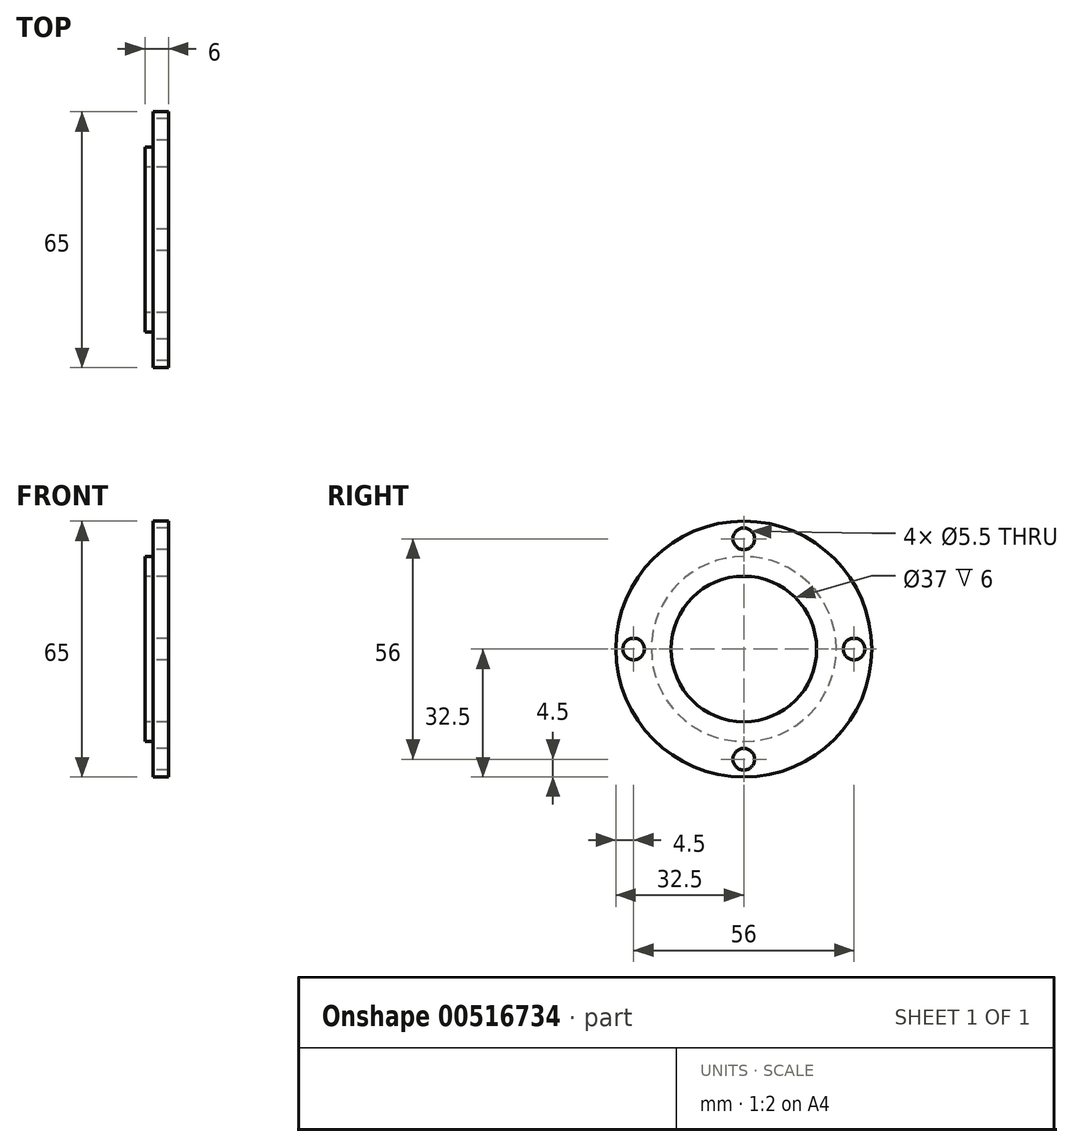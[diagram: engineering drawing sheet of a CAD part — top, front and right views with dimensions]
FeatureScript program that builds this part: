
annotation { "Feature Type Name" : "Feature", "Feature Type Description" : "" }
export const myFeature = defineFeature(function(context is Context, id is Id, definition is map)
    precondition{}
    {
        {
            var Q0;
            Q0=qCreatedBy(makeId("Front.planeOp"),FACE);
            var sketch = newSketch(context, id + "F0", { "sketchPlane" : qUnion([Q0])});
            skLineSegment(sketch, "E0", {"start": v(-34.12, 0) * mm, "end": v(37.4, 0) * mm, "construction": true});
            skLineSegment(sketch, "E1", {"start": v(0, 32.5) * mm, "end": v(0, 23.5) * mm});
            skLineSegment(sketch, "E2", {"start": v(4, 18.5) * mm, "end": v(4, 32.5) * mm});
            skLineSegment(sketch, "E3", {"start": v(4, 32.5) * mm, "end": v(0, 32.5) * mm});
            skLineSegment(sketch, "E4", {"start": v(4, 18.5) * mm, "end": v(-2, 18.5) * mm});
            skLineSegment(sketch, "E5", {"start": v(0, 23.5) * mm, "end": v(-2, 23.5) * mm});
            skLineSegment(sketch, "E6", {"start": v(-2, 23.5) * mm, "end": v(-2, 18.5) * mm});
            skSolve(sketch);
        }
        {
            var Q0;
            Q0=qSketchRegion(id+"F0",true);
            var Q1;
            Q1=sQuery(id+"F0.wireOp",EDGE,"E0");
            revolve(context, id + "F1", {"entities" : qUnion([Q0]), "axis" : qUnion([Q1]), "revolveType" : RevolveType.FULL});
        }
        {
            var Q0;
            Q0=makeQuery(id+"F1.opRevolve","SWEPT_FACE",FACE,{"disambiguationData":[OSD([sQuery(id+"F0.wireOp",EDGE,"E1")])]});
            var sketch = newSketch(context, id + "F2", { "sketchPlane" : qUnion([Q0])});
            skCircle(sketch, "E7", {"center": v(0, 0) * mm, "radius": 28 * mm, "construction": true});
            skPoint(sketch, "E8", {"position": v(0, 28) * mm});
            skPoint(sketch, "E9", {"position": v(28, 0) * mm});
            skPoint(sketch, "E10", {"position": v(0, -28) * mm});
            skPoint(sketch, "E11", {"position": v(-28, 0) * mm});
            skSolve(sketch);
        }
        {
            var Q0;
            Q0=sQuery(id+"F2.wireOp",VERTEX,"E8");
            var Q1;
            Q1=sQuery(id+"F2.wireOp",VERTEX,"E9");
            var Q2;
            Q2=sQuery(id+"F2.wireOp",VERTEX,"E10");
            var Q3;
            Q3=sQuery(id+"F2.wireOp",VERTEX,"E11");
            var Q4;
            Q4=makeQuery(id+"F1.opRevolve","SWEPT_BODY",BODY,{"disambiguationData":[OSD([sQuery(id+"F0.wireOp",EDGE,"E1"),sQuery(id+"F0.wireOp",EDGE,"tT6BRb7s-vRpj-rYgo-NGWG-NiOAgnGncPOi"),sQuery(id+"F0.wireOp",EDGE,"NPM4Fhls-3h4F-LKu2-0bDe-jooJPq9ozquu"),sQuery(id+"F0.wireOp",EDGE,"qbmVd184-m6D5-koAs-8WDn-yLaDaJsLGjF8"),sQuery(id+"F0.wireOp",EDGE,"E2"),sQuery(id+"F0.wireOp",EDGE,"E3")])]});
            hole(context, id + "F3", {"style" : HoleStyle.SIMPLE, "endStyle" : HoleEndStyle.THROUGH, "standardTappedOrClearance" : lookupTablePath({ "standard" : "ISO", "fit" : "Normal", "size" : "M5", "type" : "Clearance" }), "standardBlindInLast" : lookupTablePath({ "fit" : "Standard", "standard" : "ISO", "size" : "M5", "type" : "Clearance" }), "holeDiameter" : 5.5 * mm, "isTappedThrough" : true, "tappedDepth" : 12 * mm, "tapClearance" : 3, "locations" : qUnion([Q0, Q1, Q2, Q3]), "scope" : qUnion([Q4])});
        }
    });
